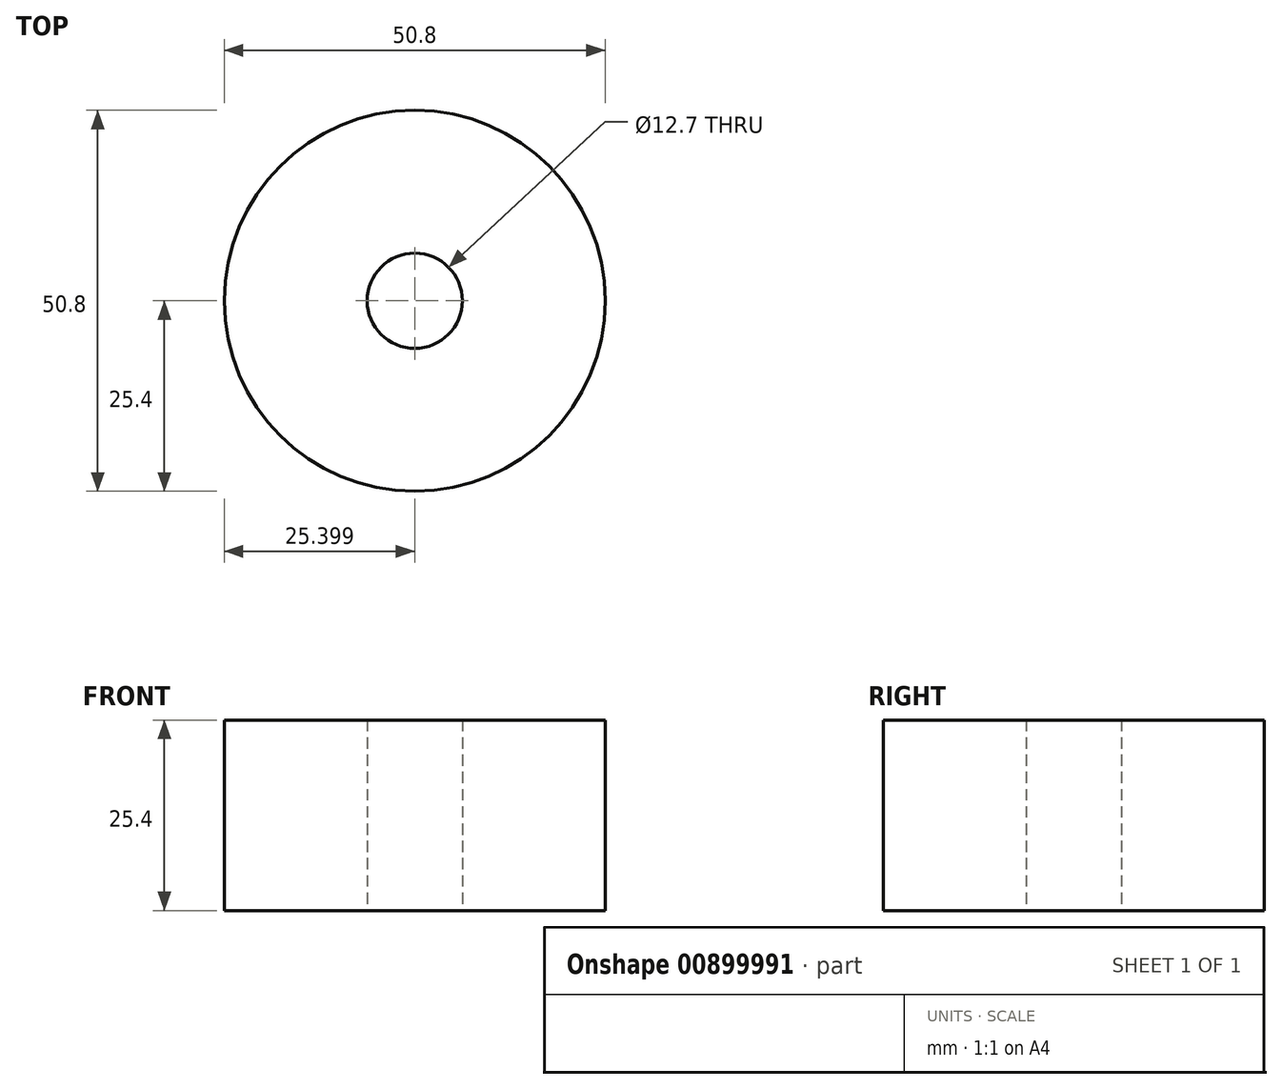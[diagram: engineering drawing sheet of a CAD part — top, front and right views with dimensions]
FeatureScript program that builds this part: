
annotation { "Feature Type Name" : "Feature", "Feature Type Description" : "" }
export const myFeature = defineFeature(function(context is Context, id is Id, definition is map)
    precondition{}
    {
        {
            var Q0;
            Q0=qCreatedBy(makeId("Top.planeOp"),FACE);
            var sketch = newSketch(context, id + "F0", { "sketchPlane" : qUnion([Q0])});
            skCircle(sketch, "E0", {"center": v(-35.14, 0) * mm, "radius": 25.4 * mm});
            skCircle(sketch, "E1", {"center": v(-35.14, 0) * mm, "radius": 6.35 * mm});
            skSolve(sketch);
        }
        {
            var Q0;
            Q0=makeQuery(id+"F0.imprint","IMPRINT",FACE,{"disambiguationData":[TD([[makeQuery(id+"F0.imprint","IMPRINT",EDGE,{"derivedFrom":sQuery(id+"F0.wireOp",EDGE,"E0")}),1.0]])]});
            extrude(context, id + "F1", {"entities" : qUnion([Q0]), "depth" : 25.4 * mm, "offsetDistance" : 25.4 * mm});
        }
    });
